# Revit family: LM0166851_Mueble Plus 140 cm con 2 Lavamanos Cascade
name_source: partatom
category: Plumbing Fixtures
units: mm (PartAtom-declared; Revit-internal decimal feet)

## family parameters
Always vertical = Yes
Cut with Voids When Loaded = No
Host = Wall
OmniClass Number = 23.45.05.14.14
OmniClass Title = Sinks/Lavatories
Part Type = Normal
Room Calculation Point = No
Round Connector Dimension = Use Diameter
Shared = No

## types (1)
- Type 1
    Acabado = Cubo
    Alto = 875 mm  [stored 2.87073 ft]
    Ancho = 1400 mm  [stored 4.59318 ft]
    Creado por = IDD
    Dimensiones generales producto (H * W * D) = 28,54” x 55,12” x 19,69” (725 x 1400 x 500 mm)
    Fabricante = Corona
    Fecha de creación = 24/07/2020
    Garantía = 5 años
    Peso Bruto aprox = 129,0 lb (58,5 kg)
    Peso Neto aprox = 116,8 lb (53 kg)
    Profundidad = 500 mm  [stored 1.64042 ft]
    Referencia = LM0166851
    Resistencia a la humedad = 8%
    URL = https://corona.co

note: [stored X ft] marks values corroborated as IEEE doubles in the binary element streams (Revit-internal decimal feet)

## geometry (parser evidence)
native form markers: Sweep x5
no freeform markers — native parametric forms only
